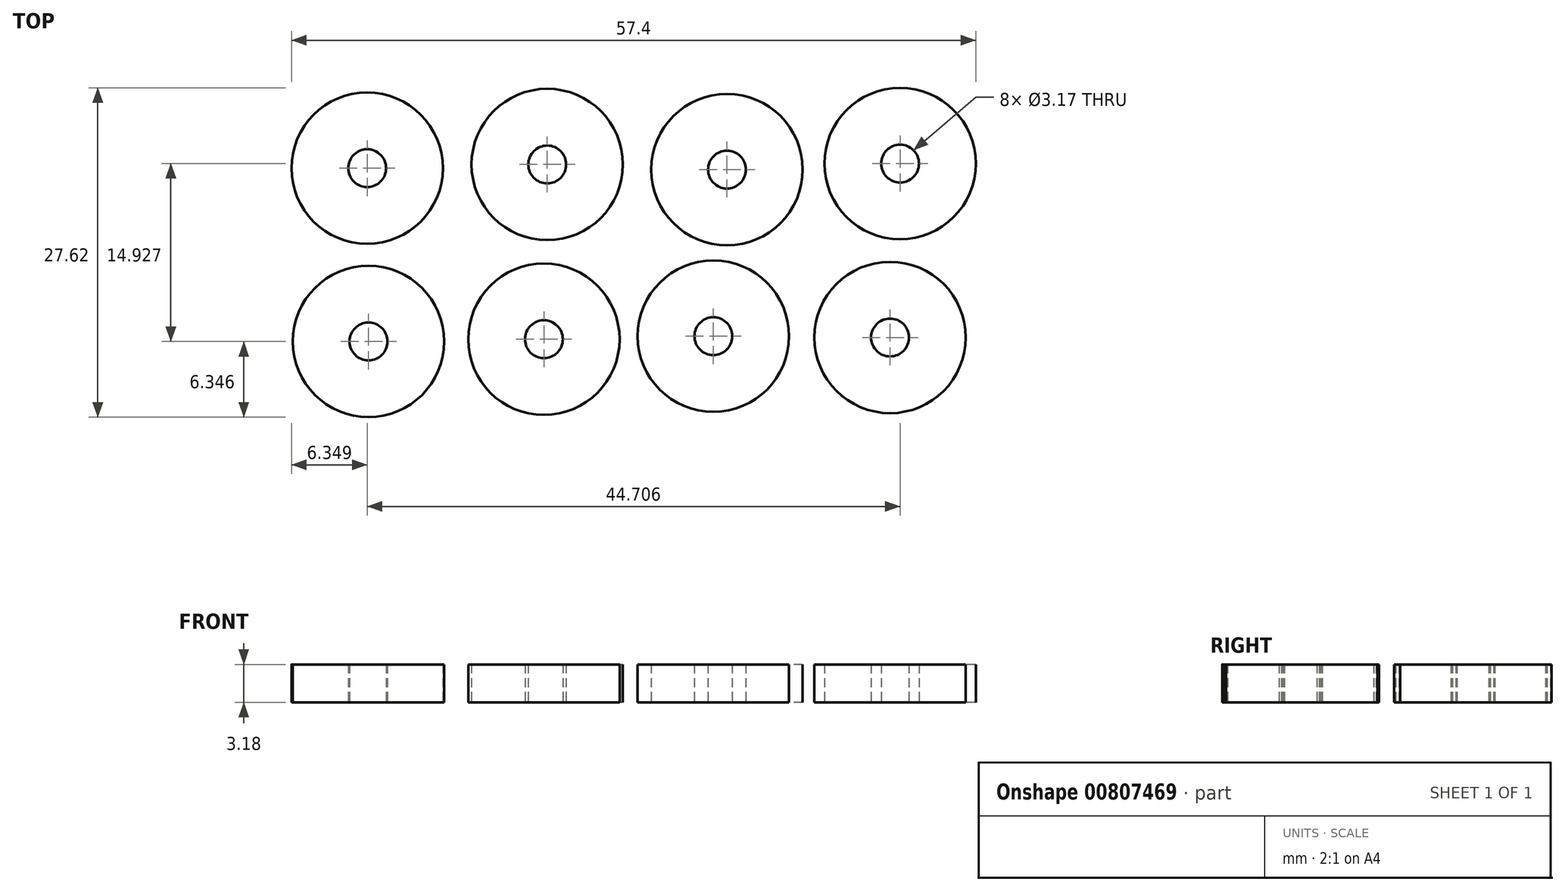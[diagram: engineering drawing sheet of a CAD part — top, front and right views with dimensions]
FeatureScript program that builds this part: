
annotation { "Feature Type Name" : "Feature", "Feature Type Description" : "" }
export const myFeature = defineFeature(function(context is Context, id is Id, definition is map)
    precondition{}
    {
        {
            var Q0;
            Q0=qCreatedBy(makeId("Top.planeOp"),FACE);
            var sketch = newSketch(context, id + "F0", { "sketchPlane" : qUnion([Q0])});
            skCircle(sketch, "E0", {"center": v(-24.6, 9.6) * mm, "radius": 6.35 * mm});
            skCircle(sketch, "E1", {"center": v(-9.5, 9.91) * mm, "radius": 6.35 * mm});
            skCircle(sketch, "E2", {"center": v(5.58, 9.49) * mm, "radius": 6.35 * mm});
            skCircle(sketch, "E3", {"center": v(20.1, 10) * mm, "radius": 6.35 * mm});
            skCircle(sketch, "E4", {"center": v(-24.49, -4.93) * mm, "radius": 6.35 * mm});
            skCircle(sketch, "E5", {"center": v(4.44, -4.49) * mm, "radius": 6.35 * mm});
            skCircle(sketch, "E6", {"center": v(-9.78, -4.75) * mm, "radius": 6.35 * mm});
            skCircle(sketch, "E7", {"center": v(19.26, -4.6) * mm, "radius": 6.35 * mm});
            skCircle(sketch, "E8", {"center": v(-24.6, 9.6) * mm, "radius": 1.59 * mm});
            skCircle(sketch, "E9", {"center": v(-9.5, 9.91) * mm, "radius": 1.59 * mm});
            skCircle(sketch, "E10", {"center": v(5.58, 9.49) * mm, "radius": 1.59 * mm});
            skCircle(sketch, "E11", {"center": v(20.1, 10) * mm, "radius": 1.59 * mm});
            skCircle(sketch, "E12", {"center": v(19.26, -4.6) * mm, "radius": 1.59 * mm});
            skCircle(sketch, "E13", {"center": v(4.44, -4.49) * mm, "radius": 1.59 * mm});
            skCircle(sketch, "E14", {"center": v(-9.78, -4.75) * mm, "radius": 1.59 * mm});
            skCircle(sketch, "E15", {"center": v(-24.49, -4.93) * mm, "radius": 1.59 * mm});
            skSolve(sketch);
        }
        {
            var Q0;
            Q0 = qSketchRegion(id + "F0", true);
            extrude(context, id + "F1", {"entities" : qUnion([Q0]), "depth" : 3.17 * mm, "offsetDistance" : 25.4 * mm});
        }
    });
